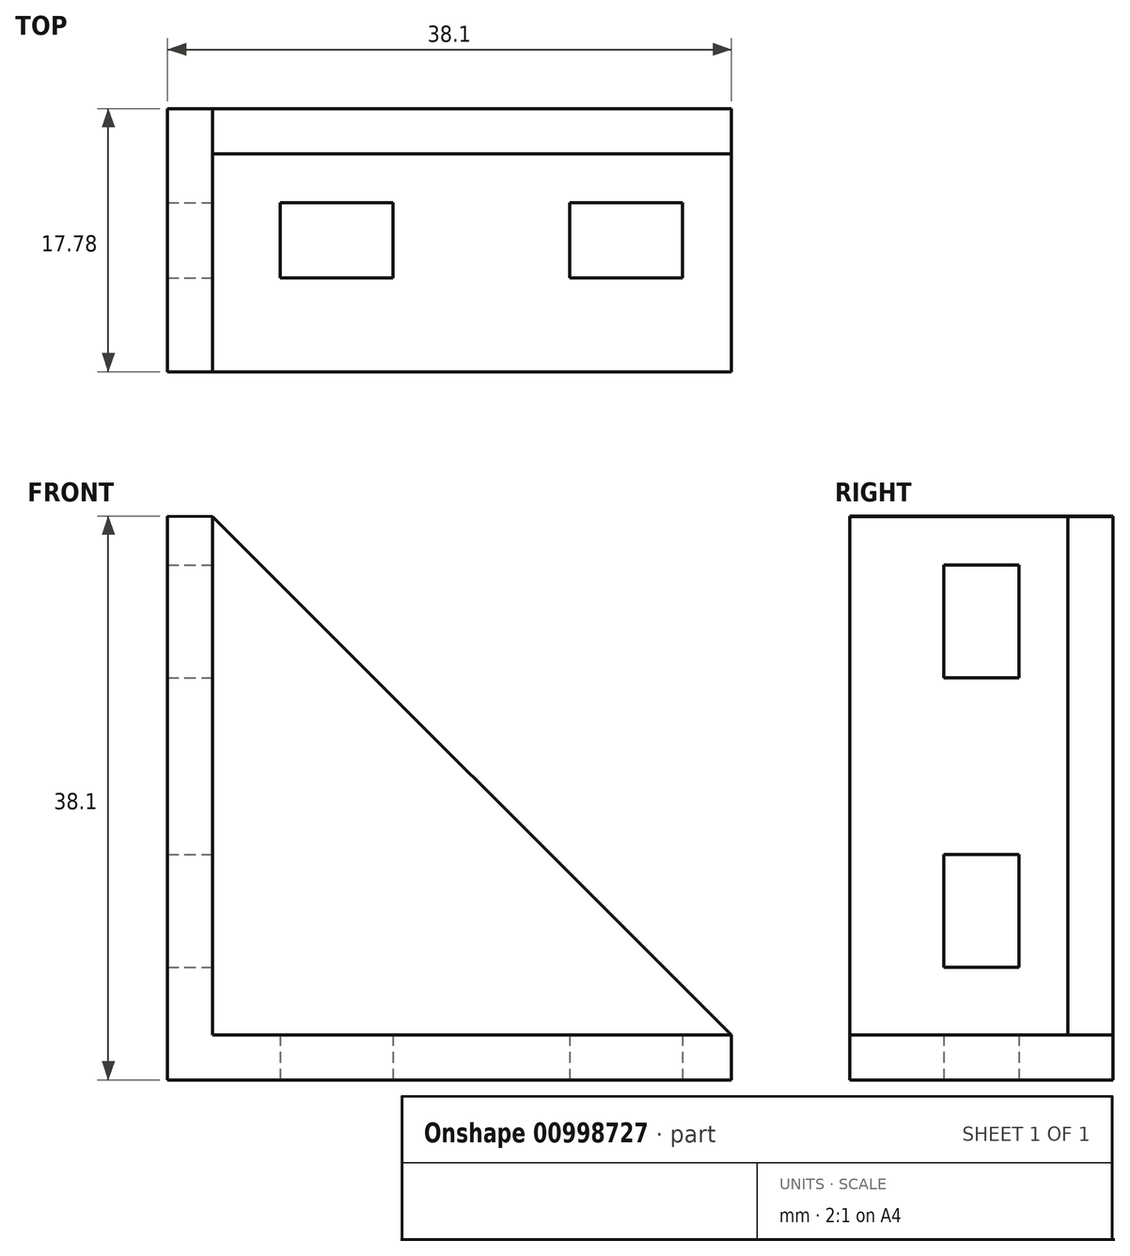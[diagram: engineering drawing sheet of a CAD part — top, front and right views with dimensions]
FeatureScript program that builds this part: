
annotation { "Feature Type Name" : "Feature", "Feature Type Description" : "" }
export const myFeature = defineFeature(function(context is Context, id is Id, definition is map)
    precondition{}
    {
        {
            var Q0;
            Q0=qCreatedBy(makeId("Front.planeOp"),FACE);
            var sketch = newSketch(context, id + "F0", { "sketchPlane" : qUnion([Q0])});
            skLineSegment(sketch, "E0", {"start": v(-36.01, 38.1) * mm, "end": v(-36.01, 0) * mm});
            skLineSegment(sketch, "E1", {"start": v(-36.01, 0) * mm, "end": v(2.09, 0) * mm});
            skLineSegment(sketch, "E2", {"start": v(2.09, 0) * mm, "end": v(2.09, 3.05) * mm});
            skLineSegment(sketch, "E3", {"start": v(2.09, 3.05) * mm, "end": v(-32.97, 3.05) * mm});
            skLineSegment(sketch, "E4", {"start": v(-32.97, 3.05) * mm, "end": v(-32.97, 38.04) * mm});
            skLineSegment(sketch, "E5", {"start": v(-32.97, 38.04) * mm, "end": v(-36.01, 38.1) * mm});
            skSolve(sketch);
        }
        {
            var Q0;
            Q0=makeQuery(id+"F0.imprint","IMPRINT",FACE,{"disambiguationData":[TD([[makeQuery(id+"F0.imprint","IMPRINT",EDGE,{"derivedFrom":sQuery(id+"F0.wireOp",EDGE,"E0")}),1.0]])]});
            extrude(context, id + "F1", {"entities" : qUnion([Q0]), "depth" : 17.78 * mm, "offsetDistance" : 25.4 * mm});
        }
        {
            var Q0;
            Q0=qCreatedBy(makeId("Front.planeOp"),FACE);
            var sketch = newSketch(context, id + "F2", { "sketchPlane" : qUnion([Q0])});
            skPoint(sketch, "E6", {"position": v(-32.97, 38.04) * mm});
            skPoint(sketch, "E7", {"position": v(2.09, 3.05) * mm});
            skLineSegment(sketch, "E8", {"start": v(-32.97, 38.04) * mm, "end": v(2.09, 3.05) * mm});
            skLineSegment(sketch, "E9", {"start": v(2.09, 3.05) * mm, "end": v(-32.97, 3.05) * mm});
            skLineSegment(sketch, "E10", {"start": v(-32.97, 3.05) * mm, "end": v(-32.97, 38.04) * mm});
            skSolve(sketch);
        }
        {
            var Q0;
            Q0=makeQuery(id+"F2.imprint","IMPRINT",FACE,{"disambiguationData":[TD([[makeQuery(id+"F2.imprint","IMPRINT",EDGE,{"derivedFrom":sQuery(id+"F2.wireOp",EDGE,"E8")}),-1.0]])]});
            extrude(context, id + "F3", {"entities" : qUnion([Q0]), "operationType" : NewBodyOperationType.ADD, "depth" : 3.05 * mm, "offsetDistance" : 25.4 * mm});
        }
        {
            var Q0;
            Q0=qCreatedBy(makeId("Right.planeOp"),FACE);
            var sketch = newSketch(context, id + "F4", { "sketchPlane" : qUnion([Q0])});
            skLineSegment(sketch, "E11.bottom", {"start": v(-11.43, 34.8) * mm, "end": v(-6.35, 34.8) * mm});
            skLineSegment(sketch, "E11.top", {"start": v(-11.43, 27.18) * mm, "end": v(-6.35, 27.18) * mm});
            skLineSegment(sketch, "E11.left", {"start": v(-11.43, 34.8) * mm, "end": v(-11.43, 27.18) * mm});
            skLineSegment(sketch, "E11.right", {"start": v(-6.35, 34.8) * mm, "end": v(-6.35, 27.18) * mm});
            skPoint(sketch, "E12", {"position": v(-11.43, 30.99) * mm});
            skPoint(sketch, "E13", {"position": v(-8.9, 34.8) * mm});
            skLineSegment(sketch, "E14.1.0.0", {"start": v(-11.43, 15.24) * mm, "end": v(-6.35, 15.24) * mm});
            skLineSegment(sketch, "E14.1.0.1", {"start": v(-6.35, 15.24) * mm, "end": v(-6.35, 7.62) * mm});
            skLineSegment(sketch, "E14.1.0.2", {"start": v(-11.43, 7.62) * mm, "end": v(-6.35, 7.62) * mm});
            skLineSegment(sketch, "E14.1.0.3", {"start": v(-11.43, 15.24) * mm, "end": v(-11.43, 7.62) * mm});
            skSolve(sketch);
        }
        {
            var Q0;
            Q0 = qSketchRegion(id + "F4", true);
            extrude(context, id + "F5", {"entities" : qUnion([Q0]), "operationType" : NewBodyOperationType.REMOVE, "oppositeDirection" : true, "depth" : 56.13 * mm, "offsetDistance" : 25.4 * mm});
        }
        {
            var Q0;
            Q0=qCreatedBy(makeId("Top.planeOp"),FACE);
            var sketch = newSketch(context, id + "F6", { "sketchPlane" : qUnion([Q0])});
            skLineSegment(sketch, "E15.bottom", {"start": v(-28.4, -6.35) * mm, "end": v(-20.77, -6.35) * mm});
            skLineSegment(sketch, "E15.top", {"start": v(-28.4, -11.43) * mm, "end": v(-20.77, -11.43) * mm});
            skLineSegment(sketch, "E15.left", {"start": v(-28.4, -6.35) * mm, "end": v(-28.4, -11.43) * mm});
            skLineSegment(sketch, "E15.right", {"start": v(-20.77, -6.35) * mm, "end": v(-20.77, -11.43) * mm});
            skLineSegment(sketch, "E16.bottom", {"start": v(-8.84, -6.35) * mm, "end": v(-1.22, -6.35) * mm});
            skLineSegment(sketch, "E16.top", {"start": v(-8.84, -11.43) * mm, "end": v(-1.22, -11.43) * mm});
            skLineSegment(sketch, "E16.left", {"start": v(-8.84, -6.35) * mm, "end": v(-8.84, -11.43) * mm});
            skLineSegment(sketch, "E16.right", {"start": v(-1.22, -6.35) * mm, "end": v(-1.22, -11.43) * mm});
            skPoint(sketch, "E17", {"position": v(-24.58, -6.35) * mm});
            skPoint(sketch, "E18", {"position": v(-28.4, -8.9) * mm});
            skPoint(sketch, "E19", {"position": v(-5.03, -6.35) * mm});
            skPoint(sketch, "E20", {"position": v(-8.84, -8.9) * mm});
            skSolve(sketch);
        }
        {
            var Q0;
            Q0 = qSketchRegion(id + "F6", true);
            extrude(context, id + "F7", {"entities" : qUnion([Q0]), "operationType" : NewBodyOperationType.REMOVE, "depth" : 25.4 * mm, "offsetDistance" : 25.4 * mm});
        }
    });
